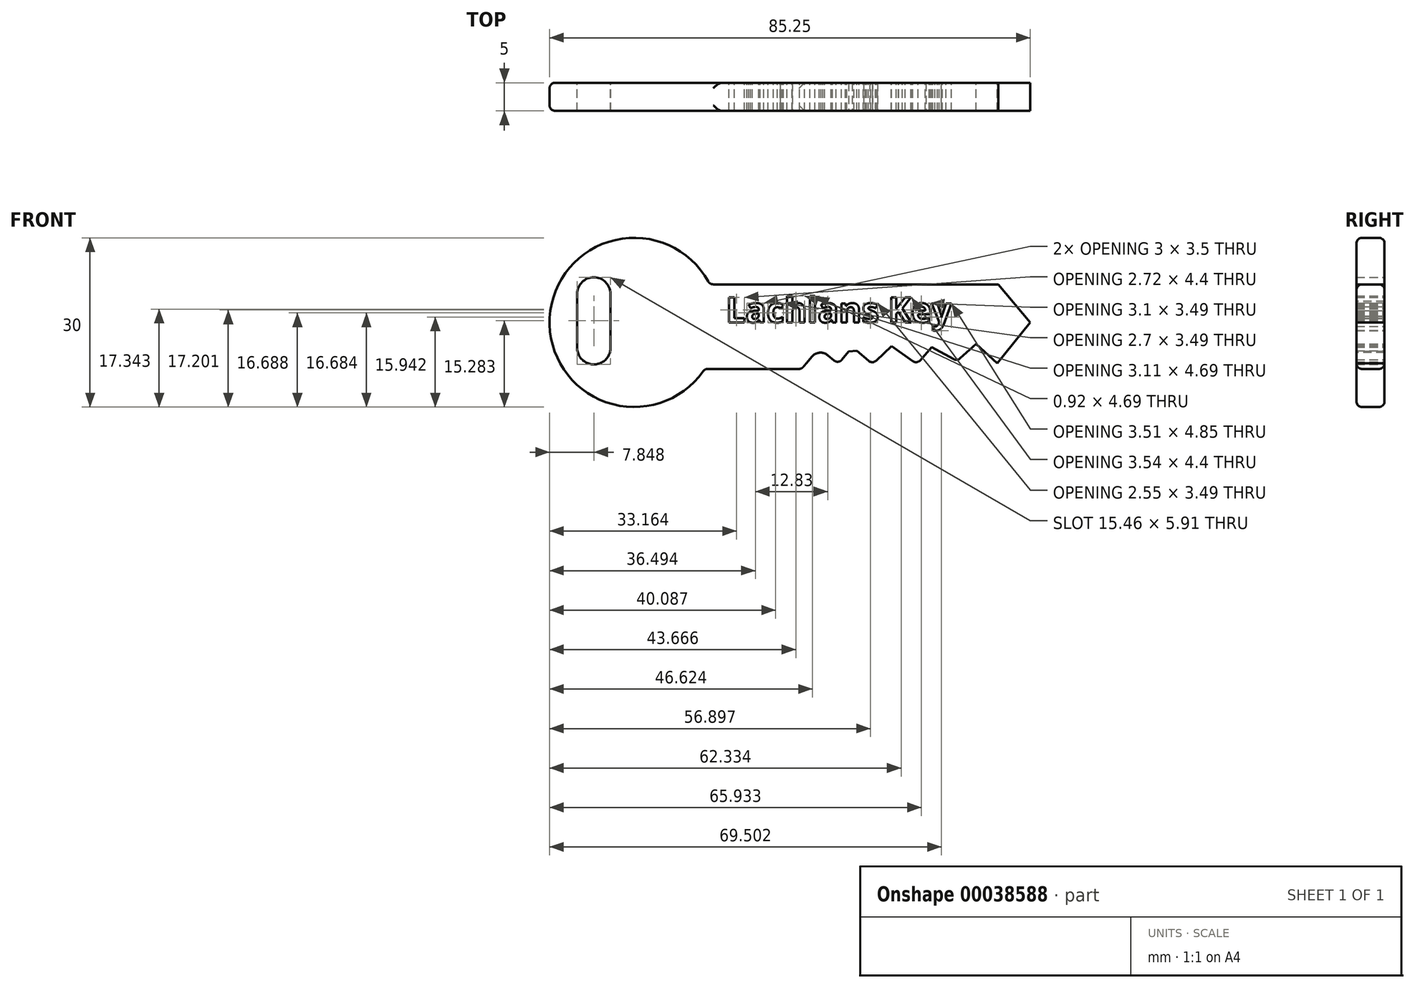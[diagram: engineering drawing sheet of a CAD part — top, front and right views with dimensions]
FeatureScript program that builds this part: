
annotation { "Feature Type Name" : "Feature", "Feature Type Description" : "" }
export const myFeature = defineFeature(function(context is Context, id is Id, definition is map)
    precondition{}
    {
        {
            var Q0;
            Q0=qCreatedBy(makeId("Front.planeOp"),FACE);
            var sketch = newSketch(context, id + "F0", { "sketchPlane" : qUnion([Q0])});
            skArc(sketch, "E0", {"start": v(13.4, 6.75) * mm, "mid": v(-14.97, 0.87) * mm, "end": v(12.53, -8.25) * mm});
            skLineSegment(sketch, "E1", {"start": v(13.4, 6.75) * mm, "end": v(64.55, 6.75) * mm});
            skLineSegment(sketch, "E2", {"start": v(64.55, 6.75) * mm, "end": v(70.25, 0) * mm});
            skLineSegment(sketch, "E3", {"start": v(70.25, 0) * mm, "end": v(64.37, -7.22) * mm});
            skLineSegment(sketch, "E4", {"start": v(64.37, -7.22) * mm, "end": v(60.62, -3.83) * mm});
            skLineSegment(sketch, "E5", {"start": v(60.62, -3.83) * mm, "end": v(57.24, -6.86) * mm});
            skLineSegment(sketch, "E6", {"start": v(57.24, -6.86) * mm, "end": v(52.78, -4.37) * mm});
            skLineSegment(sketch, "E7", {"start": v(52.78, -4.37) * mm, "end": v(50.1, -7.4) * mm});
            skLineSegment(sketch, "E8", {"start": v(50.1, -7.4) * mm, "end": v(45.65, -4.2) * mm});
            skLineSegment(sketch, "E9", {"start": v(45.65, -4.2) * mm, "end": v(42.26, -7.4) * mm});
            skLineSegment(sketch, "E10", {"start": v(42.26, -7.4) * mm, "end": v(38.7, -4.37) * mm});
            skLineSegment(sketch, "E11", {"start": v(38.7, -4.37) * mm, "end": v(36.2, -7.4) * mm});
            skLineSegment(sketch, "E12", {"start": v(36.2, -7.4) * mm, "end": v(32.8, -4.55) * mm});
            skLineSegment(sketch, "E13", {"start": v(32.8, -4.55) * mm, "end": v(29.69, -8.25) * mm});
            skLineSegment(sketch, "E14", {"start": v(29.69, -8.25) * mm, "end": v(12.53, -8.25) * mm});
            skSolve(sketch);
        }
        {
            var Q0;
            Q0=qCreatedBy(makeId("Front.planeOp"),FACE);
            var sketch = newSketch(context, id + "F1", { "sketchPlane" : qUnion([Q0])});
            skLineSegment(sketch, "E15", {"start": v(-10.1, 5.05) * mm, "end": v(-10.1, -4.48) * mm});
            skLineSegment(sketch, "E16", {"start": v(-4.2, 5.05) * mm, "end": v(-4.2, -4.1) * mm});
            skArc(sketch, "E17", {"start": v(-4.2, 5.05) * mm, "mid": v(-7.15, 8.01) * mm, "end": v(-10.1, 5.05) * mm});
            skArc(sketch, "E18", {"start": v(-10.1, -4.48) * mm, "mid": v(-6.95, -7.44) * mm, "end": v(-4.2, -4.1) * mm});
            skSolve(sketch);
        }
        {
            var Q0;
            Q0=makeQuery(id+"F0.imprint","IMPRINT",FACE,{"disambiguationData":[TD([[makeQuery(id+"F0.imprint","IMPRINT",EDGE,{"derivedFrom":sQuery(id+"F0.wireOp",EDGE,"E0")}),1.0]])]});
            extrude(context, id + "F2", {"entities" : qUnion([Q0]), "depth" : 5 * mm});
        }
        {
            var Q0;
            Q0=makeQuery(id+"F1.imprint","IMPRINT",FACE,{"disambiguationData":[TD([[makeQuery(id+"F1.imprint","IMPRINT",EDGE,{"derivedFrom":sQuery(id+"F1.wireOp",EDGE,"E15")}),1.0]])]});
            extrude(context, id + "F3", {"entities" : qUnion([Q0]), "operationType" : NewBodyOperationType.REMOVE, "depth" : 25 * mm});
        }
        {
            var Q0;
            Q0=qCreatedBy(makeId("Front.planeOp"),FACE);
            var sketch = newSketch(context, id + "F4", { "sketchPlane" : qUnion([Q0])});
            skText(sketch, "E19", { "text": "Lachlans Key", "fontName": "OpenSans-Bold.ttf"});
            const initialGuessF4  = {"E19": [0.01625, 0, 1, 0, 0.00444]};
            skSetInitialGuess(sketch, initialGuessF4);
            skSolve(sketch);
        }
        {
            var Q0;
            Q0 = qSketchRegion(id + "F4", true);
            extrude(context, id + "F5", {"entities" : qUnion([Q0]), "operationType" : NewBodyOperationType.REMOVE, "depth" : 25 * mm});
        }
        {
            var Q0;
            Q0=makeQuery(id+"F2.opExtrude","SWEPT_FACE",FACE,{"disambiguationData":[OSD([sQuery(id+"F0.wireOp",EDGE,"E14")])]});
            var Q1;
            Q1=makeQuery(id+"F2.opExtrude","SWEPT_FACE",FACE,{"disambiguationData":[OSD([sQuery(id+"F0.wireOp",EDGE,"E0")])]});
            fillet(context, id + "F6", {"entities" : qUnion([Q0, Q1]), "radius" : 1 * mm, "tangentPropagation" : true, "allowEdgeOverflow" : false});
        }
        {
            var Q0;
            Q0=makeQuery(id+"F2.opExtrude","SWEPT_EDGE",EDGE,{"disambiguationData":[OSD([sQuery(id+"F0.wireOp",EDGE,"E12"),sQuery(id+"F0.wireOp",EDGE,"E13")])]});
            fillet(context, id + "F7", {"entities" : qUnion([Q0]), "radius" : 2 * mm, "tangentPropagation" : true, "allowEdgeOverflow" : false});
        }
        {
            var Q0;
            Q0=makeQuery(id+"F2.opExtrude","SWEPT_EDGE",EDGE,{"disambiguationData":[OSD([sQuery(id+"F0.wireOp",EDGE,"E11"),sQuery(id+"F0.wireOp",EDGE,"E12")])]});
            var Q1;
            Q1=makeQuery(id+"F2.opExtrude","SWEPT_EDGE",EDGE,{"disambiguationData":[OSD([sQuery(id+"F0.wireOp",EDGE,"E9"),sQuery(id+"F0.wireOp",EDGE,"E10")])]});
            var Q2;
            Q2=makeQuery(id+"F2.opExtrude","SWEPT_EDGE",EDGE,{"disambiguationData":[OSD([sQuery(id+"F0.wireOp",EDGE,"E7"),sQuery(id+"F0.wireOp",EDGE,"E8")])]});
            var Q3;
            Q3=makeQuery(id+"F2.opExtrude","SWEPT_EDGE",EDGE,{"disambiguationData":[OSD([sQuery(id+"F0.wireOp",EDGE,"E5"),sQuery(id+"F0.wireOp",EDGE,"E6")])]});
            fillet(context, id + "F8", {"entities" : qUnion([Q0, Q1, Q2, Q3]), "radius" : 1 * mm, "tangentPropagation" : true, "allowEdgeOverflow" : false});
        }
        {
            var Q0;
            Q0=makeQuery(id+"F2.opExtrude","SWEPT_EDGE",EDGE,{"disambiguationData":[OSD([sQuery(id+"F0.wireOp",EDGE,"E10"),sQuery(id+"F0.wireOp",EDGE,"E11")])]});
            chamfer(context, id + "F9", {"entities" : qUnion([Q0]), "width" : 1 * mm, "tangentPropagation" : true});
        }
    });
